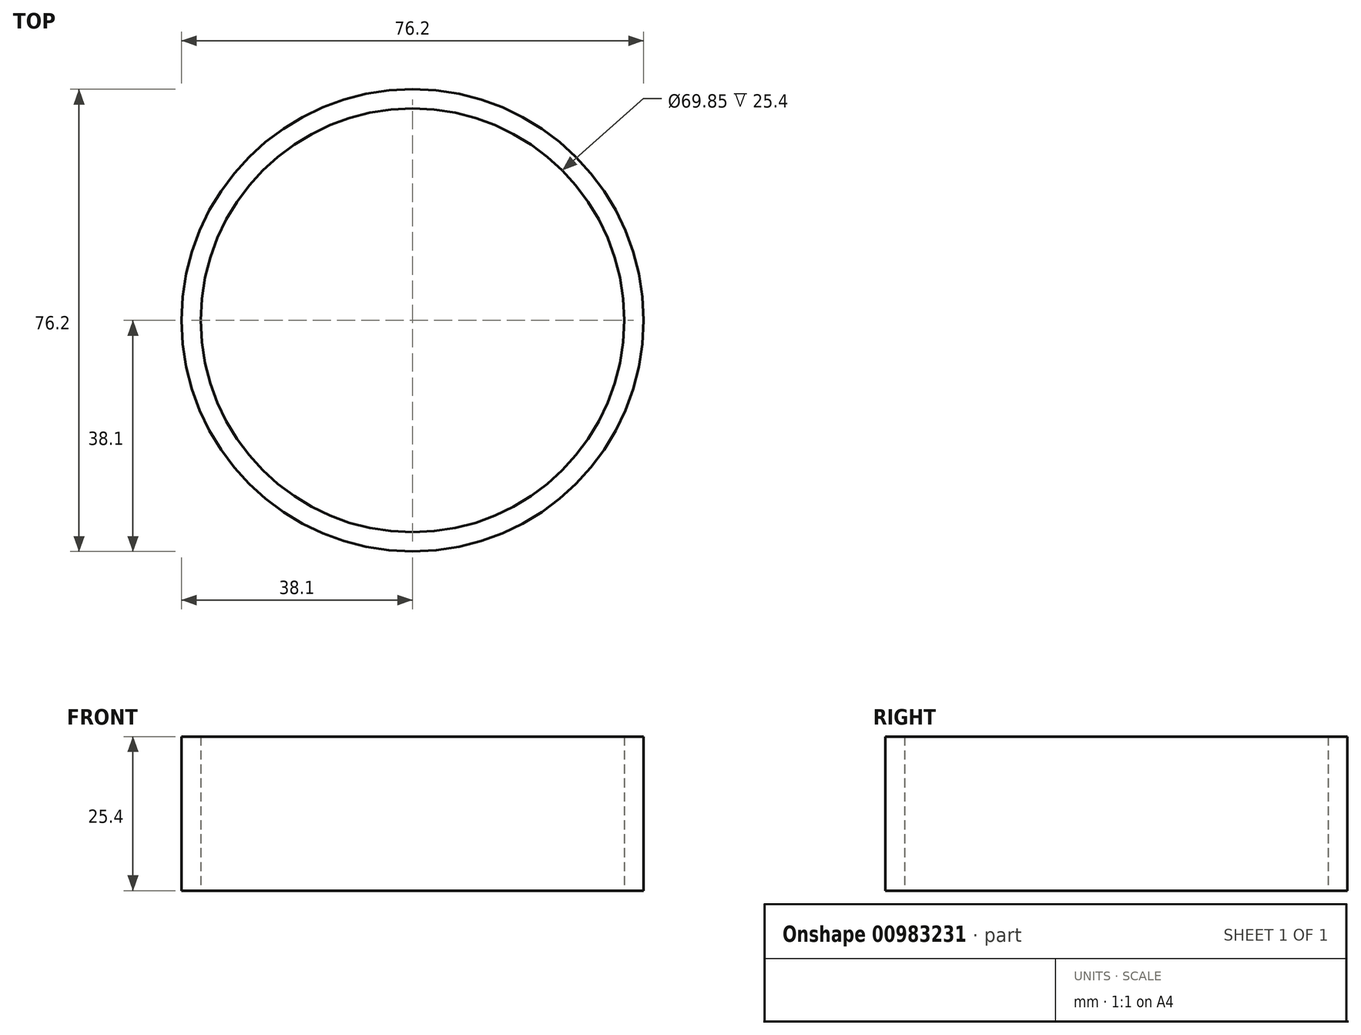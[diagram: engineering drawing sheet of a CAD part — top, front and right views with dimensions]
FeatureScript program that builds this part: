
annotation { "Feature Type Name" : "Feature", "Feature Type Description" : "" }
export const myFeature = defineFeature(function(context is Context, id is Id, definition is map)
    precondition{}
    {
        {
            var Q0;
            Q0=qCreatedBy(makeId("Top.planeOp"),FACE);
            var sketch = newSketch(context, id + "F0", { "sketchPlane" : qUnion([Q0])});
            skCircle(sketch, "E0", {"center": v(0, 0) * mm, "radius": 38.1 * mm});
            skCircle(sketch, "E1", {"center": v(0, 0) * mm, "radius": 34.93 * mm});
            skSolve(sketch);
        }
        {
            var Q0;
            Q0=makeQuery(id+"F0.imprint","IMPRINT",FACE,{"disambiguationData":[TD([[makeQuery(id+"F0.imprint","IMPRINT",EDGE,{"derivedFrom":sQuery(id+"F0.wireOp",EDGE,"E0")}),1.0]])]});
            extrude(context, id + "F1", {"entities" : qUnion([Q0]), "depth" : 25.4 * mm, "offsetDistance" : 25.4 * mm});
        }
    });
